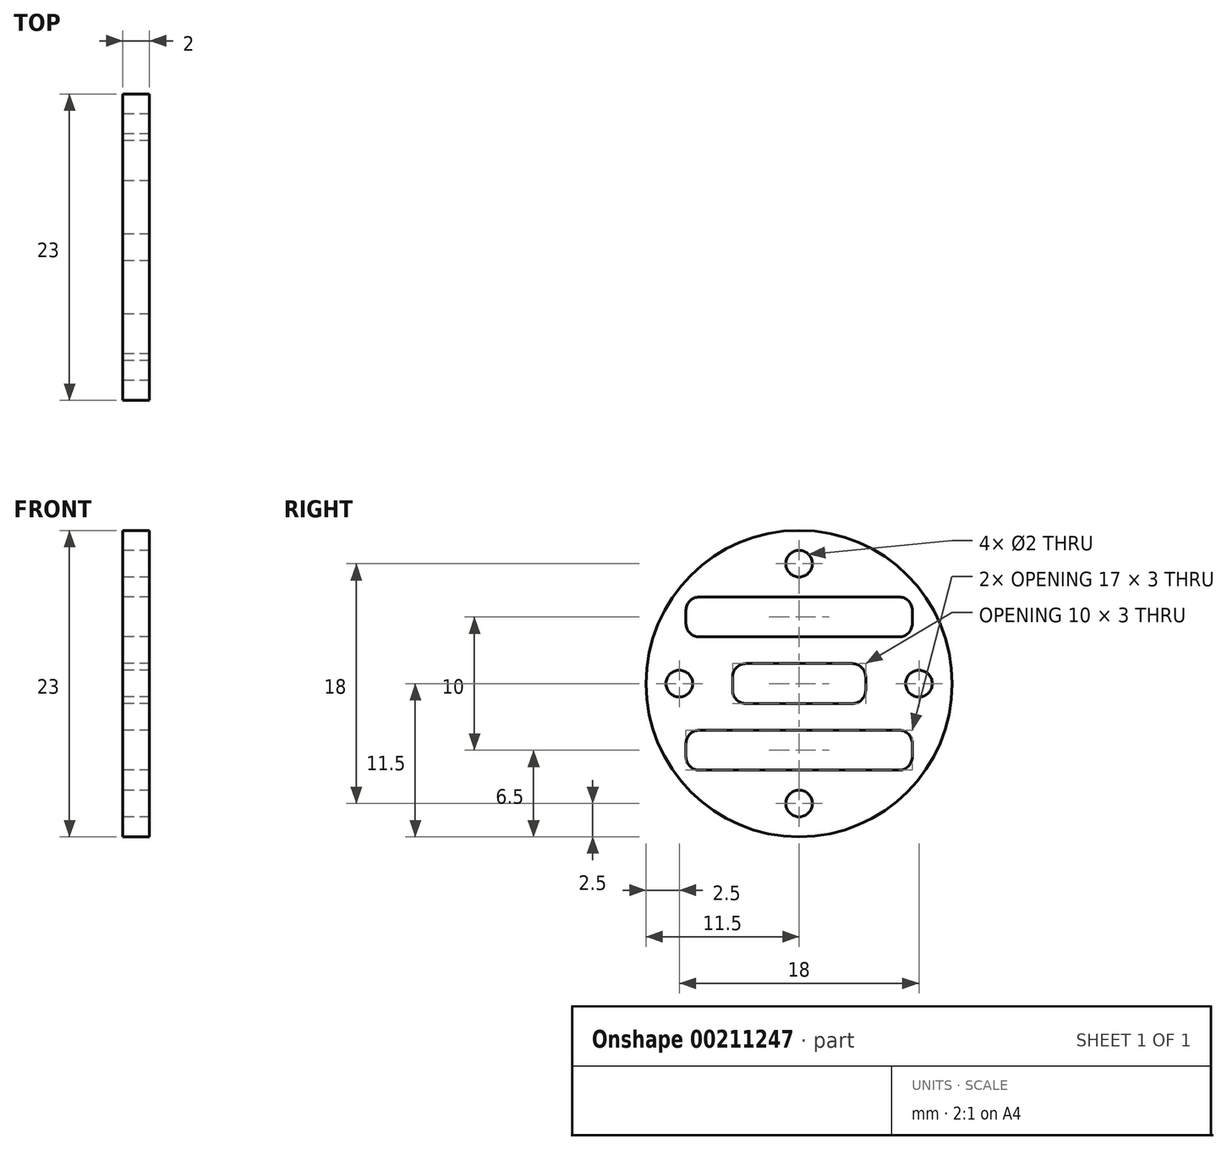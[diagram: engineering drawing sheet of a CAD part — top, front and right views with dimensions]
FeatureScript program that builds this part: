
annotation { "Feature Type Name" : "Feature", "Feature Type Description" : "" }
export const myFeature = defineFeature(function(context is Context, id is Id, definition is map)
    precondition{}
    {
        {
            var Q0;
            Q0=qCreatedBy(makeId("Right.planeOp"),FACE);
            var sketch = newSketch(context, id + "F0", { "sketchPlane" : qUnion([Q0])});
            skCircle(sketch, "E0", {"center": v(0, 0) * mm, "radius": 11.5 * mm});
            skCircle(sketch, "E1", {"center": v(0, 0) * mm, "radius": 9 * mm, "construction": true});
            skCircle(sketch, "E2", {"center": v(0, 9) * mm, "radius": 1 * mm});
            skCircle(sketch, "E3", {"center": v(9, 0) * mm, "radius": 1 * mm});
            skCircle(sketch, "E4", {"center": v(0, -9) * mm, "radius": 1 * mm});
            skCircle(sketch, "E5", {"center": v(-9, 0) * mm, "radius": 1 * mm});
            skLineSegment(sketch, "E6", {"start": v(-11.33, 5) * mm, "end": v(12.29, 5) * mm, "construction": true});
            skLineSegment(sketch, "E7", {"start": v(-12.66, -5) * mm, "end": v(13.02, -5) * mm, "construction": true});
            skLineSegment(sketch, "E8", {"start": v(0, 14.72) * mm, "end": v(0, -15.83) * mm, "construction": true});
            skLineSegment(sketch, "E9.bottom", {"start": v(-8.5, 6.5) * mm, "end": v(8.5, 6.5) * mm});
            skLineSegment(sketch, "E9.top", {"start": v(-8.5, 3.5) * mm, "end": v(8.5, 3.5) * mm});
            skLineSegment(sketch, "E9.left", {"start": v(-8.5, 6.5) * mm, "end": v(-8.5, 3.5) * mm});
            skLineSegment(sketch, "E9.right", {"start": v(8.5, 6.5) * mm, "end": v(8.5, 3.5) * mm});
            skPoint(sketch, "E9.middle", {"position": v(0, 5) * mm});
            skLineSegment(sketch, "E10.bottom", {"start": v(-8.5, -3.5) * mm, "end": v(8.5, -3.5) * mm});
            skLineSegment(sketch, "E10.top", {"start": v(-8.5, -6.5) * mm, "end": v(8.5, -6.5) * mm});
            skLineSegment(sketch, "E10.left", {"start": v(-8.5, -3.5) * mm, "end": v(-8.5, -6.5) * mm});
            skLineSegment(sketch, "E10.right", {"start": v(8.5, -3.5) * mm, "end": v(8.5, -6.5) * mm});
            skPoint(sketch, "E10.middle", {"position": v(0, -5) * mm});
            skLineSegment(sketch, "E11.bottom", {"start": v(-5, 1.5) * mm, "end": v(5, 1.5) * mm});
            skLineSegment(sketch, "E11.top", {"start": v(-5, -1.5) * mm, "end": v(5, -1.5) * mm});
            skLineSegment(sketch, "E11.left", {"start": v(-5, 1.5) * mm, "end": v(-5, -1.5) * mm});
            skLineSegment(sketch, "E11.right", {"start": v(5, 1.5) * mm, "end": v(5, -1.5) * mm});
            skSolve(sketch);
        }
        {
            var Q0;
            Q0=qSketchRegion(id+"F0",true);
            extrude(context, id + "F1", {"entities" : qUnion([Q0]), "depth" : 2 * mm});
        }
        {
            var Q0;
            Q0=makeQuery(id+"F1.opExtrude","SWEPT_EDGE",EDGE,{"disambiguationData":[OSD([sQuery(id+"F0.wireOp",EDGE,"E9.bottom"),sQuery(id+"F0.wireOp",EDGE,"E9.left")])]});
            var Q1;
            Q1=makeQuery(id+"F1.opExtrude","SWEPT_EDGE",EDGE,{"disambiguationData":[OSD([sQuery(id+"F0.wireOp",EDGE,"E9.top"),sQuery(id+"F0.wireOp",EDGE,"E9.left")])]});
            var Q2;
            Q2=makeQuery(id+"F1.opExtrude","SWEPT_EDGE",EDGE,{"disambiguationData":[OSD([sQuery(id+"F0.wireOp",EDGE,"E9.bottom"),sQuery(id+"F0.wireOp",EDGE,"E9.right")])]});
            var Q3;
            Q3=makeQuery(id+"F1.opExtrude","SWEPT_EDGE",EDGE,{"disambiguationData":[OSD([sQuery(id+"F0.wireOp",EDGE,"E9.top"),sQuery(id+"F0.wireOp",EDGE,"E9.right")])]});
            var Q4;
            Q4=makeQuery(id+"F1.opExtrude","SWEPT_EDGE",EDGE,{"disambiguationData":[OSD([sQuery(id+"F0.wireOp",EDGE,"E11.top"),sQuery(id+"F0.wireOp",EDGE,"E11.right")])]});
            var Q5;
            Q5=makeQuery(id+"F1.opExtrude","SWEPT_EDGE",EDGE,{"disambiguationData":[OSD([sQuery(id+"F0.wireOp",EDGE,"E11.top"),sQuery(id+"F0.wireOp",EDGE,"E11.left")])]});
            var Q6;
            Q6=makeQuery(id+"F1.opExtrude","SWEPT_EDGE",EDGE,{"disambiguationData":[OSD([sQuery(id+"F0.wireOp",EDGE,"E10.top"),sQuery(id+"F0.wireOp",EDGE,"E10.left")])]});
            var Q7;
            Q7=makeQuery(id+"F1.opExtrude","SWEPT_EDGE",EDGE,{"disambiguationData":[OSD([sQuery(id+"F0.wireOp",EDGE,"E10.top"),sQuery(id+"F0.wireOp",EDGE,"E10.right")])]});
            var Q8;
            Q8=makeQuery(id+"F1.opExtrude","SWEPT_EDGE",EDGE,{"disambiguationData":[OSD([sQuery(id+"F0.wireOp",EDGE,"E11.bottom"),sQuery(id+"F0.wireOp",EDGE,"E11.left")])]});
            var Q9;
            Q9=makeQuery(id+"F1.opExtrude","SWEPT_EDGE",EDGE,{"disambiguationData":[OSD([sQuery(id+"F0.wireOp",EDGE,"E10.bottom"),sQuery(id+"F0.wireOp",EDGE,"E10.left")])]});
            var Q10;
            Q10=makeQuery(id+"F1.opExtrude","SWEPT_EDGE",EDGE,{"disambiguationData":[OSD([sQuery(id+"F0.wireOp",EDGE,"E10.bottom"),sQuery(id+"F0.wireOp",EDGE,"E10.right")])]});
            var Q11;
            Q11=makeQuery(id+"F1.opExtrude","SWEPT_EDGE",EDGE,{"disambiguationData":[OSD([sQuery(id+"F0.wireOp",EDGE,"E11.bottom"),sQuery(id+"F0.wireOp",EDGE,"E11.right")])]});
            fillet(context, id + "F2", {"entities" : qUnion([Q0, Q1, Q2, Q3, Q4, Q5, Q6, Q7, Q8, Q9, Q10, Q11]), "radius" : 1 * mm, "tangentPropagation" : true, "allowEdgeOverflow" : false});
        }
    });
